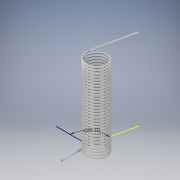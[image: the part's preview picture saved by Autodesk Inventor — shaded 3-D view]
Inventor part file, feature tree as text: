
AUTODESK INVENTOR PART (.ipt)
format: ipt  version: 2018 (Build 220112000, 112)  size: 482,304 bytes
history: native  units: in
note: dims shown in document units (in); Inventor stores cm internally (conversion verified against a paired STEP export)
features: sketch x4, extrude x2, helix x1
ambient origin geometry x8: Origin, YZ Plane, XZ Plane, XY Plane, X Axis, Y Axis, Z Axis, Center Point
bodies: Solid1 (feature_tree)
feature tree (7):
  helix  "Coil1"  [1 undecoded]
  extrude  "Extrusion1"  Depth=0.35in TaperAngle=0.0deg
  extrude  "Extrusion2"  Depth=0.2in
  sketch  "Sketch4"
  sketch  "Sketch1"  dims[d1=0.0875in]
  sketch  "Sketch2"  dims[d2=1.0in d3=0.67in d4=11.8243in d5=0.0in d6=90.0deg d7=90.0deg d8=0.0in d9=0.0in d10=0.35in d11=0.0in]
  sketch  "Sketch3"  dims[d12=0.2in d13=0.0in d14=0.7018in]
note: 1 required parameter value undecoded (feature->parameter linkage not recoverable at this tier; creation-order binding heuristic only, values carry confidence <= 0.55)
